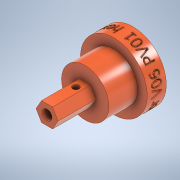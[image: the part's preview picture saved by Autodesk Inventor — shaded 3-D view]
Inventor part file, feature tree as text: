
AUTODESK INVENTOR PART (.ipt)
format: ipt  version: 2022.2 (Build 262287010, 287A)  size: 1,412,096 bytes
history: native  units: in
note: dims shown in document units (in); Inventor stores cm internally (conversion verified against a paired STEP export)
features: sketch x6, extrude x3, hole x2, plane x1, emboss x1
ambient origin geometry x8: Origin, YZ Plane, XZ Plane, XY Plane, X Axis, Y Axis, Z Axis, Center Point
bodies: Solid1 (feature_tree)
feature tree (13):
  extrude  "Extrusion1"  Depth=1.0in TaperAngle=0.0deg
  extrude  "Extrusion2"  Depth=0.75in TaperAngle=0.0deg
  extrude  "Extrusion3"  Depth=0.5in TaperAngle=0.0deg
  hole  "Hole1"  [1 undecoded]
  hole  "Hole2"  [1 undecoded]
  plane  "Work Plane1"
  emboss  "Emboss2"
  sketch  "Sketch1"  dims[d0=0.5in d1=1.0in d2=0.0in]
  sketch  "Sketch2"  dims[d3=1.24in d4=0.75in d5=0.0in]
  sketch  "Sketch3"  dims[d6=1.75in d7=0.5in d8=0.0in]
  sketch  "Sketch6"  dims[d13=0.244in]
  sketch  "Sketch7"  dims[d14=0.17in d15=0.75in d16=0.5in d17=0.093in d18=0.5635in d19=1.0in d20=0.8108in]
  sketch  "Sketch8"  dims[d21=0.249in d22=0.75in d23=0.26in d24=0.2411in d25=0.5635in d26=0.31in d27=0.0in d28=0.1in d29=0.0in]
note: 2 required parameter values undecoded (feature->parameter linkage not recoverable at this tier; creation-order binding heuristic only, values carry confidence <= 0.55)
